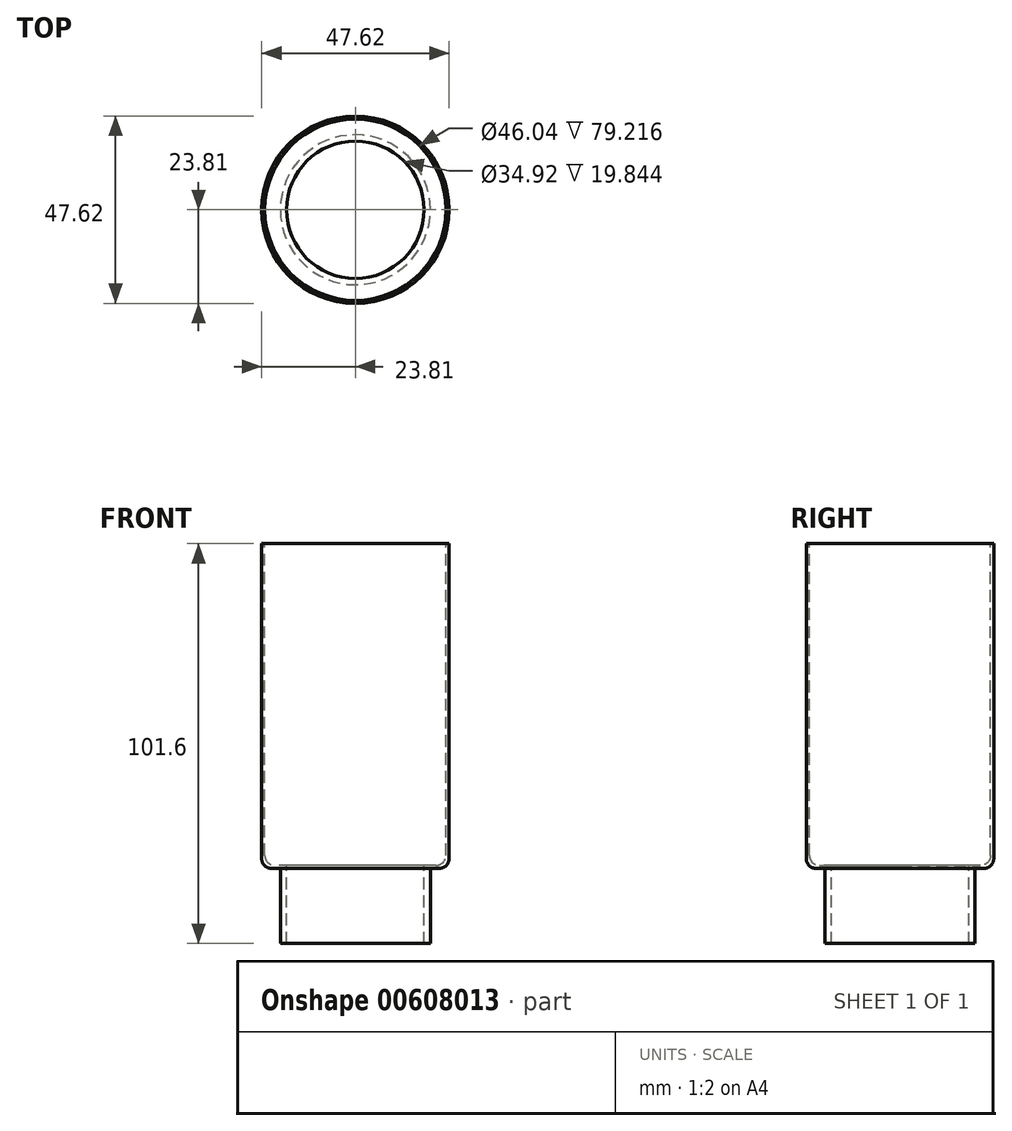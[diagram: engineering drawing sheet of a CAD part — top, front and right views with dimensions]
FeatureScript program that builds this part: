
annotation { "Feature Type Name" : "Feature", "Feature Type Description" : "" }
export const myFeature = defineFeature(function(context is Context, id is Id, definition is map)
    precondition{}
    {
        {
            var Q0;
            Q0=qCreatedBy(makeId("Front.planeOp"),FACE);
            var sketch = newSketch(context, id + "F0", { "sketchPlane" : qUnion([Q0])});
            skLineSegment(sketch, "E0", {"start": v(19.05, 0) * mm, "end": v(19.05, 19.05) * mm});
            skLineSegment(sketch, "E1", {"start": v(19.05, 19.05) * mm, "end": v(21.27, 19.05) * mm});
            skLineSegment(sketch, "E2", {"start": v(23.81, 21.6) * mm, "end": v(23.81, 101.6) * mm});
            skLineSegment(sketch, "E3", {"start": v(23.81, 101.6) * mm, "end": v(23.02, 101.6) * mm});
            skLineSegment(sketch, "E4", {"start": v(23.02, 101.6) * mm, "end": v(23.02, 22.38) * mm});
            skLineSegment(sketch, "E5", {"start": v(20.48, 19.84) * mm, "end": v(17.46, 19.84) * mm});
            skLineSegment(sketch, "E6", {"start": v(17.46, 19.84) * mm, "end": v(17.46, 0) * mm});
            skLineSegment(sketch, "E7", {"start": v(17.46, 0) * mm, "end": v(19.05, 0) * mm});
            skPoint(sketch, "E8.visualSharp", {"position": v(23.02, 19.84) * mm});
            skArc(sketch, "E8.filletArc", {"start": v(20.48, 19.84) * mm, "mid": v(22.27, 20.59) * mm, "end": v(23.02, 22.38) * mm});
            skPoint(sketch, "E9.visualSharp", {"position": v(23.81, 19.05) * mm});
            skArc(sketch, "E9.filletArc", {"start": v(21.27, 19.05) * mm, "mid": v(23.07, 19.8) * mm, "end": v(23.81, 21.59) * mm});
            skLineSegment(sketch, "E10", {"start": v(0, 95.14) * mm, "end": v(0, -87.78) * mm, "construction": true});
            skSolve(sketch);
        }
        {
            var Q0;
            Q0 = qSketchRegion(id + "F0", true);
            var Q1;
            Q1=sQuery(id+"F0.wireOp",EDGE,"E10");
            revolve(context, id + "F1", {"entities" : qUnion([Q0]), "axis" : qUnion([Q1]), "revolveType" : RevolveType.FULL});
        }
    });
